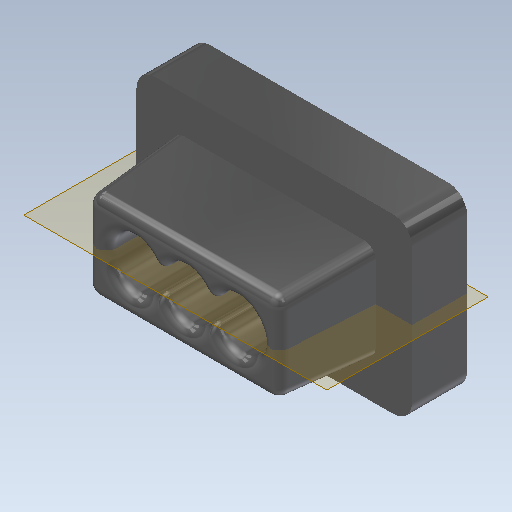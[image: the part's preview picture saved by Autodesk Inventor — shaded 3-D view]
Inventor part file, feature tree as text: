
AUTODESK INVENTOR PART (.ipt)
format: ipt  version: 2020 (Build 240168000, 168)  size: 225,280 bytes
history: native  units: in
note: dims shown in document units (in); Inventor stores cm internally (conversion verified against a paired STEP export)
features: extrude x3, sketch x3, fillet x2, plane x1
ambient origin geometry x8: Origin, YZ Plane, XZ Plane, XY Plane, X Axis, Y Axis, Z Axis, Center Point
bodies: Solid1 (feature_tree)
feature tree (9):
  extrude  "Extrusion1"  Depth=0.185in
  extrude  "Extrusion2"  Depth=0.217in
  fillet  "Fillet1"  Radius=0.106in
  extrude  "Extrusion3"  Depth=0.02in
  fillet  "Fillet2"  Radius=0.098in
  plane  "Work Plane1"
  sketch  "Sketch1"  dims[d0=0.295in d1=0.185in]
  sketch  "Sketch2"  dims[d2=0.059in d3=0.0in d4=0.217in d5=0.106in]
  sketch  "Sketch3"  dims[d6=0.098in d7=-0.0236in d8=0.02in d9=0.098in d10=0.0in d11=0.012in]
